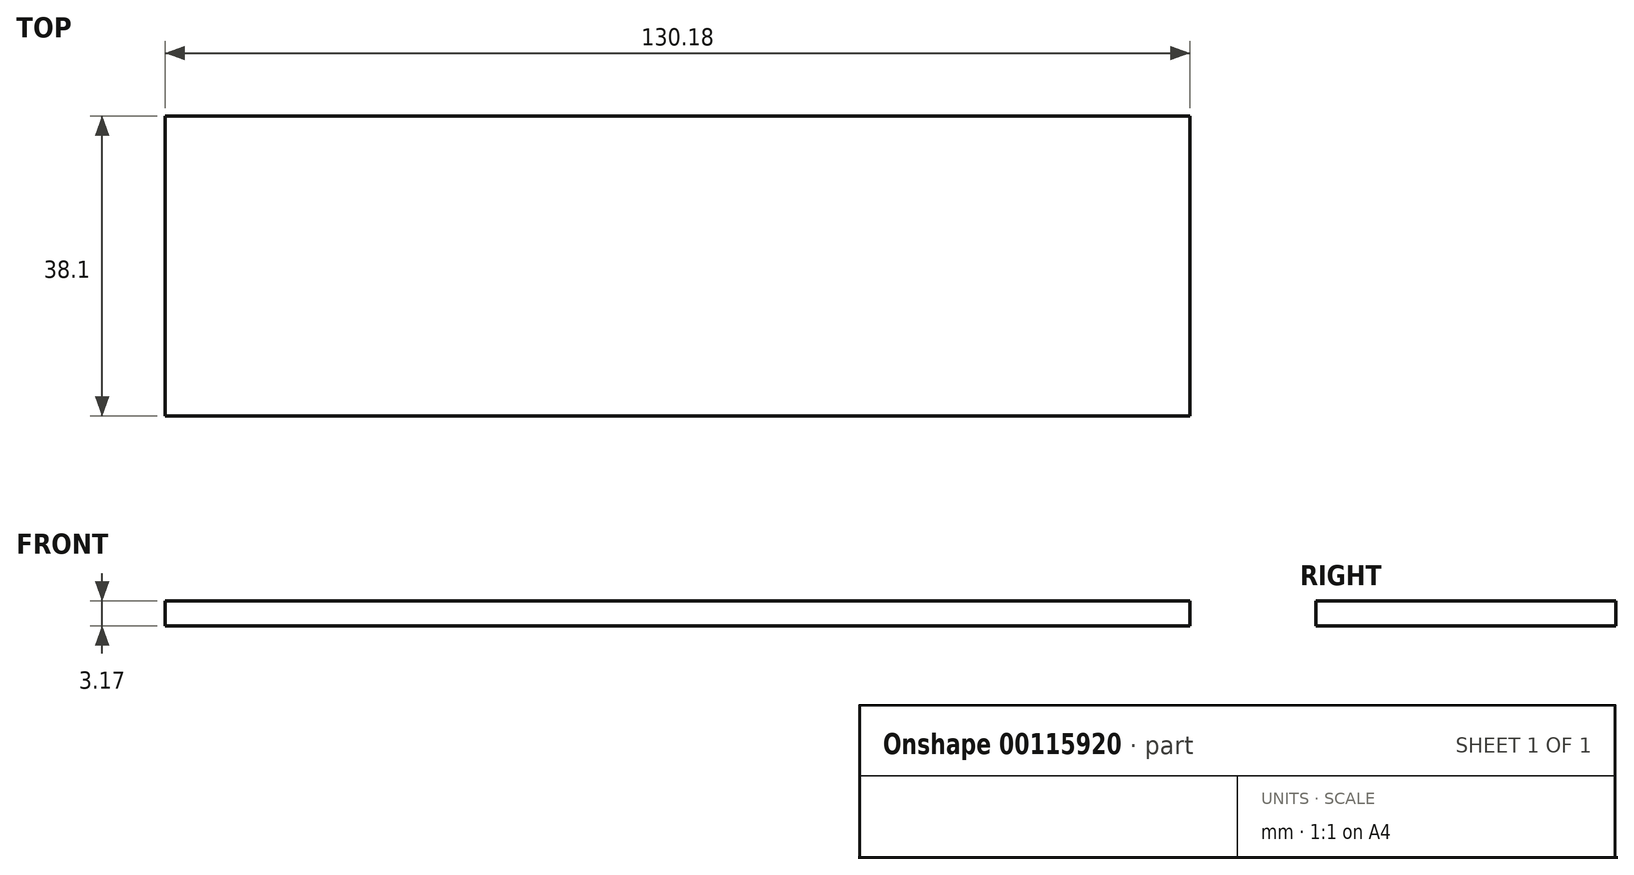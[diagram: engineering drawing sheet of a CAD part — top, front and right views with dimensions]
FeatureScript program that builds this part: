
annotation { "Feature Type Name" : "Feature", "Feature Type Description" : "" }
export const myFeature = defineFeature(function(context is Context, id is Id, definition is map)
    precondition{}
    {
        {
            var Q0;
            Q0=qCreatedBy(makeId("Top.planeOp"),FACE);
            var sketch = newSketch(context, id + "F0", { "sketchPlane" : qUnion([Q0])});
            skLineSegment(sketch, "E0.bottom", {"start": v(-24.43, 28.53) * mm, "end": v(105.75, 28.53) * mm});
            skLineSegment(sketch, "E0.top", {"start": v(-24.43, -9.57) * mm, "end": v(105.75, -9.57) * mm});
            skLineSegment(sketch, "E0.left", {"start": v(-24.43, 28.53) * mm, "end": v(-24.43, -9.57) * mm});
            skLineSegment(sketch, "E0.right", {"start": v(105.75, 28.53) * mm, "end": v(105.75, -9.57) * mm});
            skSolve(sketch);
        }
        {
            var Q0;
            Q0=makeQuery(id+"F0.imprint","IMPRINT",FACE,{"disambiguationData":[TD([[makeQuery(id+"F0.imprint","IMPRINT",EDGE,{"derivedFrom":sQuery(id+"F0.wireOp",EDGE,"E0.bottom")}),-1.0]])]});
            extrude(context, id + "F1", {"entities" : qUnion([Q0]), "depth" : 3.17 * mm});
        }
    });
